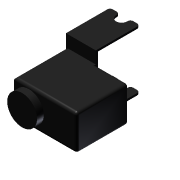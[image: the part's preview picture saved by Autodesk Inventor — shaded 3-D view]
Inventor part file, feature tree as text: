
AUTODESK INVENTOR PART (.ipt)
format: ipt  version: 2012 (Build 160160000, 160)  size: 175,104 bytes
history: native  units: mm
features: sketch x5, extrude x5, fillet x1
ambient origin geometry x8: Origin, YZ Plane, XZ Plane, XY Plane, X Axis, Y Axis, Z Axis, Center Point
bodies: Solid1 (feature_tree)
feature tree (11):
  sketch  "Sketch1"  dims[d0=24.25mm d1=43.35mm]
  extrude  "Extrusion1"  Depth=43.35mm
  extrude  "Extrusion2"  Depth=11.0mm
  extrude  "Extrusion3"  Depth=26.0mm TaperAngle=0.0deg
  extrude  "Extrusion4"  Depth=5.0mm TaperAngle=0.0deg
  extrude  "Extrusion5"  Depth=22.0mm
  fillet  "Fillet1"  Radius=41.0mm
  sketch  "Sketch2"  dims[d2=11.0mm d3=11.0mm]
  sketch  "Sketch3"  dims[d4=5.0mm d5=26.0mm d6=0.0mm]
  sketch  "Sketch4"  dims[d8=22.0mm d9=5.0mm d10=0.0mm]
  sketch  "Sketch5"  dims[d13=20.5mm d14=22.0mm d15=41.0mm d16=1.5mm d17=1.5mm d18=1.5mm d19=0.0mm d20=1.5mm d21=1.5mm d22=35.0mm d23=0.0mm d24=35.0mm d25=0.0mm d26=2.0mm]
